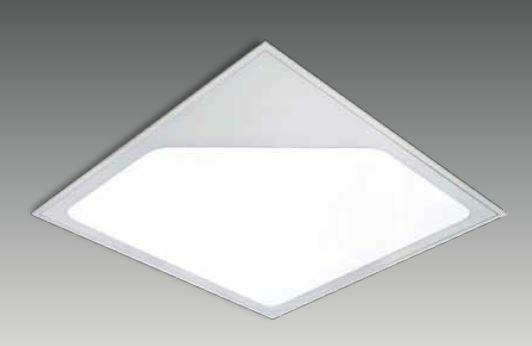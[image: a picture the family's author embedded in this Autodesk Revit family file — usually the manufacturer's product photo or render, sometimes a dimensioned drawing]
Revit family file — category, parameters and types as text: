
# Revit family: G 6060 COR
name_source: partatom
category: Lighting Fixtures
revit_build: Autodesk Revit 2017 (Build: 20160225_1515(x64)
units: mm (PartAtom-declared; Revit-internal decimal feet)

## family parameters
Always vertical = Yes
Cut with Voids When Loaded = No
Host = Ceiling
Light Source = Yes
OmniClass Number = 23.80.70.11
OmniClass Title = Luminaries for Internal Lighting
Part Type = Normal
Room Calculation Point = No
Round Connector Dimension = Use Diameter
Shared = No

## types (4) — shared parameters
Color Filter = 16777215
Dimming Lamp Color Temperature Shift = <None>
Emit Shape Visible in Rendering = Yes
Emit from Rectangle Length = 570 mm  [stored 1.87008 ft]
Emit from Rectangle Width = 570 mm  [stored 1.87008 ft]
Light Source Symbol Size = 610 mm
Manufacturer = ARLIGHT
Type Image = G 6060 COR.JPG

## per-type parameters (varying)
| type | Wattage Comments |
| GCOR.6060.36.30 | 36 |
| GCOR.6060.36.40 | 36 |
| GCOR.6060.28.30 | 28 |
| GCOR.6060.28.40 | 28 |

note: [stored X ft] marks values corroborated as IEEE doubles in the binary element streams (Revit-internal decimal feet)

## geometry (parser evidence)
native form markers: Sweep x2
no freeform markers — native parametric forms only
